# Revit family: Haworth_Fronzoni64_Table
name_source: partatom
category: Furniture
revit_build: Autodesk Revit 2018 (Build: 20170223_1515(x64)
units: mm (PartAtom-declared; Revit-internal decimal feet)

## family parameters
Always vertical = Yes
Cut with Voids When Loaded = No
OmniClass Number = 23.40.70.14.64.21
OmniClass Title = Systems Furniture
Room Calculation Point = No
Shared = No
Work Plane-Based = No

## types (3) — shared parameters
Actual Depth = 39 1/4"
Assembly Code = E2020200
Chamfer = 1/16"
Glide Height = 1/8"
Glide Offset = 13/32"
Leg Thickness = 13/16"
Manufacturer = Haworth
Product Page URL = http://www.haworth.com
Revision Number = 4
Size = Verify Final Dim. w/ Haworth
Table Top Thickness = 1"
URL = http://www.haworth.com
Warranty = http://www.haworth.com

## per-type parameters (varying)
| type | Actual Height | Actual Width | Description | High Rectangle | High Square | Low Square | Model |
| HZZE-FZHR - High Rectangle | 27 1/2" | 78 3/4" | Haworth Fronzoni '64 Table - High Rectangle | Yes | No | No | HZZE-FZHR |
| HZZE-FZHQ - High Square | 27 1/2" | 39 1/4" | Haworth Fronzoni '64 Table - High Square | No | Yes | No | HZZE-FZHQ |
| HZZE-FZLQ - Low Square | 11 3/4" | 39 1/4" | Haworth Fronzoni '64 Table - Low Square | No | No | Yes | HZZE-FZLQ |

## geometry (parser evidence)
native form markers: Sweep x2
no freeform markers — native parametric forms only
